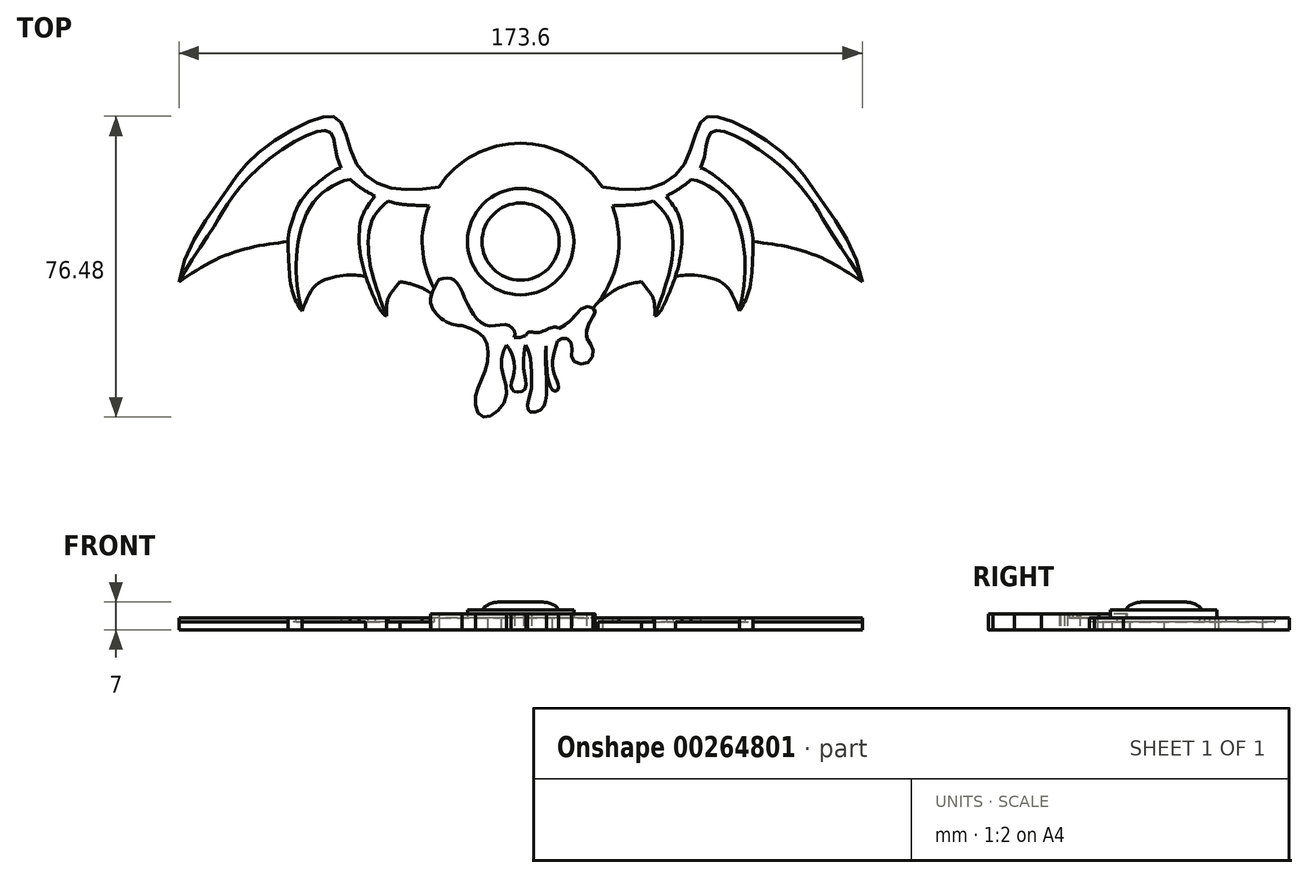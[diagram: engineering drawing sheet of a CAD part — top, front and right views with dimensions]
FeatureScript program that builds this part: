
annotation { "Feature Type Name" : "Feature", "Feature Type Description" : "" }
export const myFeature = defineFeature(function(context is Context, id is Id, definition is map)
    precondition{}
    {
        {
            var Q0;
            Q0=qCreatedBy(makeId("Top.planeOp"),FACE);
            var sketch = newSketch(context, id + "F0", { "sketchPlane" : qUnion([Q0])});
            skCircle(sketch, "E0", {"center": v(0, 0) * mm, "radius": 25 * mm});
            skLineSegment(sketch, "E1", {"start": v(0, 25) * mm, "end": v(0, -25) * mm, "construction": true});
            skFitSpline(sketch, "E2", {"points": [v(20.76, 13.92) * mm, v(34.08, 13.92) * mm, v(42, 20.48) * mm, v(46, 30.69) * mm, v(50.93, 31.48) * mm, v(67.03, 22.24) * mm, v(75.74, 11.46) * mm, v(86.8, -10.28) * mm], "startDerivative": vector(95.75, -17.53) * mm, "endDerivative": vector(18.54, -135.11) * mm});
            skFitSpline(sketch, "E3", {"points": [v(20.7, -14) * mm, v(37, -10.54) * mm, v(45, -8.07) * mm, v(66.66, 1.74) * mm, v(75.74, 11.46) * mm], "startDerivative": vector(59.46, -0.59) * mm, "endDerivative": vector(18.77, 28.66) * mm, "construction": true});
            skFitSpline(sketch, "E4", {"points": [v(23.3, 9.08) * mm, v(33.72, 10.28) * mm, v(45.64, 18.76) * mm, v(47.9, 27.18) * mm, v(51.1, 28.14) * mm, v(65.44, 19.69) * mm, v(74.45, 9.58) * mm, v(78.2, 3.43) * mm, v(86.8, -10.28) * mm], "startDerivative": vector(110.38, 5.87) * mm, "endDerivative": vector(40.39, -81.17) * mm});
            skFitSpline(sketch, "E5", {"points": [v(33.72, 10.28) * mm, v(37.86, 5.02) * mm, v(38.5, -3.9) * mm, v(37, -10.54) * mm, v(34.08, -18.9) * mm], "startDerivative": vector(21.3, -19.5) * mm, "endDerivative": vector(-13.55, -34.2) * mm});
            skFitSpline(sketch, "E6", {"points": [v(37, 11.6) * mm, v(40.25, 6.46) * mm, v(40.52, -4.24) * mm, v(37.2, -14.33) * mm, v(34.08, -18.9) * mm], "startDerivative": vector(14.85, -22) * mm, "endDerivative": vector(-16.96, -5.17) * mm});
            skFitSpline(sketch, "E7", {"points": [v(32.11, -12.01) * mm, v(33.72, -14.49) * mm, v(34.08, -18.9) * mm], "startDerivative": vector(4.43, -5.79) * mm, "endDerivative": vector(-0.15, -8.8) * mm});
            skFitSpline(sketch, "E8", {"points": [v(45.64, 18.76) * mm, v(50.26, 15.97) * mm, v(55.72, 10.44) * mm, v(58.9, 2) * mm, v(59.02, -2.64) * mm, v(58.1, -12.2) * mm, v(55.56, -17.62) * mm], "startDerivative": vector(28.21, -5.42) * mm, "endDerivative": vector(-19.1, -30.2) * mm});
            skFitSpline(sketch, "E9", {"points": [v(43.34, 15.84) * mm, v(49.55, 13.02) * mm, v(53.96, 7.9) * mm, v(56.67, -1.36) * mm, v(56.83, -10.28) * mm, v(55.56, -17.62) * mm], "startDerivative": vector(32.47, -4.35) * mm, "endDerivative": vector(-7.91, -36.84) * mm});
            skFitSpline(sketch, "E10", {"points": [v(38.97, -9.94) * mm, v(46.63, -10.28) * mm, v(52.84, -13.22) * mm, v(55.56, -17.62) * mm], "startDerivative": vector(21.38, 0.7) * mm, "endDerivative": vector(7.12, -15.9) * mm, "construction": true});
            skFitSpline(sketch, "E11", {"points": [v(59.1, 0) * mm, v(68, -1.36) * mm, v(77.72, -4.7) * mm, v(86.8, -10.28) * mm], "startDerivative": vector(27.78, -3.23) * mm, "endDerivative": vector(25.67, -17.5) * mm});
            skFitSpline(sketch, "E12", {"points": [v(19.62, -15.5) * mm, v(25.1, -11.72) * mm, v(30.69, -10.12) * mm], "startDerivative": vector(10.4, 8.3) * mm, "endDerivative": vector(11.78, 2.35) * mm});
            skFitSpline(sketch, "E13", {"points": [v(32.11, -12.01) * mm, v(30.69, -10.12) * mm], "startDerivative": vector(-1.42, 1.9) * mm, "endDerivative": vector(-1.42, 1.9) * mm});
            skFitSpline(sketch, "E14", {"points": [v(55.56, -17.62) * mm, v(52.05, -11.08) * mm, v(46.6, -8.83) * mm, v(42.13, -8.5) * mm, v(39.36, -8.79) * mm], "startDerivative": vector(-10.96, 25.87) * mm, "endDerivative": vector(-14.04, -2.02) * mm});
            skFitSpline(sketch, "E15", {"points": [v(20.76, 13.92) * mm, v(16.18, 9.49) * mm, v(19.62, -15.5) * mm], "startDerivative": vector(-16.85, -9.2) * mm, "endDerivative": vector(11.44, -45.62) * mm});
            skFitSpline(sketch, "E16.MirrorCS", {"points": [v(-20.76, 13.92) * mm, v(-16.18, 9.49) * mm, v(-19.62, -15.5) * mm], "startDerivative": vector(16.85, -9.2) * mm, "endDerivative": vector(-11.44, -45.62) * mm});
            skFitSpline(sketch, "E17.MirrorCS", {"points": [v(-23.3, 9.08) * mm, v(-33.72, 10.28) * mm, v(-45.64, 18.76) * mm, v(-47.9, 27.18) * mm, v(-51.1, 28.14) * mm, v(-65.44, 19.69) * mm, v(-74.45, 9.58) * mm, v(-78.2, 3.43) * mm, v(-86.8, -10.28) * mm], "startDerivative": vector(-110.38, 5.87) * mm, "endDerivative": vector(-40.39, -81.17) * mm});
            skFitSpline(sketch, "E18.MirrorCS", {"points": [v(-20.76, 13.92) * mm, v(-34.08, 13.92) * mm, v(-42, 20.48) * mm, v(-46, 30.69) * mm, v(-50.93, 31.48) * mm, v(-67.03, 22.24) * mm, v(-75.74, 11.46) * mm, v(-86.8, -10.28) * mm], "startDerivative": vector(-95.75, -17.53) * mm, "endDerivative": vector(-18.54, -135.11) * mm});
            skFitSpline(sketch, "E19.MirrorCS", {"points": [v(-33.72, 10.28) * mm, v(-37.86, 5.02) * mm, v(-38.5, -3.9) * mm, v(-37, -10.54) * mm, v(-34.08, -18.9) * mm], "startDerivative": vector(-21.3, -19.5) * mm, "endDerivative": vector(13.55, -34.2) * mm});
            skFitSpline(sketch, "E20.MirrorCS", {"points": [v(-37, 11.6) * mm, v(-40.25, 6.46) * mm, v(-40.52, -4.24) * mm, v(-37.2, -14.33) * mm, v(-34.08, -18.9) * mm], "startDerivative": vector(-14.85, -22) * mm, "endDerivative": vector(16.96, -5.17) * mm});
            skFitSpline(sketch, "E21.MirrorCS", {"points": [v(-43.34, 15.84) * mm, v(-49.55, 13.02) * mm, v(-53.96, 7.9) * mm, v(-56.67, -1.36) * mm, v(-56.83, -10.28) * mm, v(-55.56, -17.62) * mm], "startDerivative": vector(-32.47, -4.35) * mm, "endDerivative": vector(7.91, -36.84) * mm});
            skFitSpline(sketch, "E22.MirrorCS", {"points": [v(-45.64, 18.76) * mm, v(-50.26, 15.97) * mm, v(-55.72, 10.44) * mm, v(-58.9, 2) * mm, v(-59.02, -2.64) * mm, v(-58.1, -12.2) * mm, v(-55.56, -17.62) * mm], "startDerivative": vector(-28.21, -5.42) * mm, "endDerivative": vector(19.1, -30.2) * mm});
            skFitSpline(sketch, "E23.MirrorCS", {"points": [v(-19.62, -15.5) * mm, v(-25.1, -11.72) * mm, v(-30.69, -10.12) * mm], "startDerivative": vector(-10.4, 8.3) * mm, "endDerivative": vector(-11.78, 2.35) * mm});
            skFitSpline(sketch, "E24.MirrorCS", {"points": [v(-32.11, -12.01) * mm, v(-30.69, -10.12) * mm], "startDerivative": vector(1.42, 1.9) * mm, "endDerivative": vector(1.42, 1.9) * mm});
            skFitSpline(sketch, "E25.MirrorCS", {"points": [v(-32.11, -12.01) * mm, v(-33.72, -14.49) * mm, v(-34.08, -18.9) * mm], "startDerivative": vector(-4.43, -5.79) * mm, "endDerivative": vector(0.15, -8.8) * mm});
            skFitSpline(sketch, "E26.MirrorCS", {"points": [v(-59.1, 0) * mm, v(-68, -1.36) * mm, v(-77.72, -4.7) * mm, v(-86.8, -10.28) * mm], "startDerivative": vector(-27.78, -3.23) * mm, "endDerivative": vector(-25.67, -17.5) * mm});
            skFitSpline(sketch, "E27.MirrorCS", {"points": [v(-55.56, -17.62) * mm, v(-52.05, -11.08) * mm, v(-46.6, -8.83) * mm, v(-42.13, -8.5) * mm, v(-39.36, -8.79) * mm], "startDerivative": vector(10.96, 25.87) * mm, "endDerivative": vector(14.04, -2.02) * mm});
            skSolve(sketch);
        }
        {
            var Q0;
            {var subQ0=sQuery(id+"F0.wireOp",EDGE,"E15");Q0=makeQuery(id+"F0.imprint","IMPRINT",FACE,{"disambiguationData":[TD([[makeQuery(id+"F0.imprint","IMPRINT",EDGE,{"derivedFrom":subQ0}),-1.0]])]});}
            var Q1;
            {var subQ0=sQuery(id+"F0.wireOp",EDGE,"E15");Q1=makeQuery(id+"F0.imprint","IMPRINT",FACE,{"disambiguationData":[TD([[makeQuery(id+"F0.imprint","IMPRINT",EDGE,{"derivedFrom":subQ0}),1.0]])]});}
            var Q2;
            {var subQ0=sQuery(id+"F0.wireOp",EDGE,"E16.MirrorCS");Q2=makeQuery(id+"F0.imprint","IMPRINT",FACE,{"disambiguationData":[TD([[makeQuery(id+"F0.imprint","IMPRINT",EDGE,{"derivedFrom":subQ0}),-1.0]])]});}
            extrude(context, id + "F1", {"entities" : qUnion([Q0, Q1, Q2]), "depth" : 3 * mm, "offsetDistance" : 25 * mm});
        }
        {
            var Q0;
            Q0=qCreatedBy(makeId("Top.planeOp"),FACE);
            var sketch = newSketch(context, id + "F2", { "sketchPlane" : qUnion([Q0])});
            skCircle(sketch, "E28", {"center": v(0, 0) * mm, "radius": 13.5 * mm});
            skSolve(sketch);
        }
        {
            var Q0;
            Q0=qSketchRegion(id+"F2",true);
            extrude(context, id + "F3", {"entities" : qUnion([Q0]), "operationType" : NewBodyOperationType.ADD, "depth" : 5 * mm, "offsetDistance" : 25 * mm});
        }
        {
            var Q0;
            Q0=qCreatedBy(makeId("Top.planeOp"),FACE);
            var sketch = newSketch(context, id + "F4", { "sketchPlane" : qUnion([Q0])});
            skCircle(sketch, "E29", {"center": v(0, 0) * mm, "radius": 9.8 * mm});
            skSolve(sketch);
        }
        {
            var Q0;
            Q0=qSketchRegion(id+"F4",true);
            var Q1;
            Q1=qConstructionFilter(qBodyType(qCreatedBy(id+"F4",EDGE),BodyType.WIRE),ConstructionObject.NO);
            extrude(context, id + "F5", {"entities" : qUnion([Q0]), "operationType" : NewBodyOperationType.ADD, "surfaceEntities" : qUnion([Q1]), "depth" : 7 * mm, "offsetDistance" : 25 * mm});
        }
        {
            var Q0;
            Q0=makeQuery(id+"F5.opExtrude","CAP_FACE",FACE,{"disambiguationData":[OSD([sQuery(id+"F4.wireOp",EDGE,"E29")])],"isStart":false});
            fillet(context, id + "F6", {"entities" : qUnion([Q0]), "radius" : 5 * mm, "tangentPropagation" : true, "allowEdgeOverflow" : false});
        }
        {
            var Q0;
            {var subQ4=sQuery(id+"F0.wireOp",EDGE,"E2");Q0=makeQuery(id+"F0.imprint","IMPRINT",FACE,{"disambiguationData":[TD([[makeQuery(id+"F0.imprint","IMPRINT",EDGE,{"derivedFrom":subQ4}),-1.0]])]});}
            var Q1;
            {var subQ0=sQuery(id+"F0.wireOp",EDGE,"E15");Q1=makeQuery(id+"F0.imprint","IMPRINT",FACE,{"disambiguationData":[TD([[makeQuery(id+"F0.imprint","IMPRINT",EDGE,{"derivedFrom":subQ0}),1.0]])]});}
            var Q2;
            {var subQ0=sQuery(id+"F0.wireOp",EDGE,"E5");Q2=makeQuery(id+"F0.imprint","IMPRINT",FACE,{"disambiguationData":[TD([[makeQuery(id+"F0.imprint","IMPRINT",EDGE,{"derivedFrom":subQ0}),-1.0]])]});}
            var Q3;
            {var subQ0=sQuery(id+"F0.wireOp",EDGE,"E5");Q3=makeQuery(id+"F0.imprint","IMPRINT",FACE,{"disambiguationData":[TD([[makeQuery(id+"F0.imprint","IMPRINT",EDGE,{"derivedFrom":subQ0}),1.0]])]});}
            var Q4;
            {var subQ3=sQuery(id+"F0.wireOp",EDGE,"E9");Q4=makeQuery(id+"F0.imprint","IMPRINT",FACE,{"disambiguationData":[TD([[makeQuery(id+"F0.imprint","IMPRINT",EDGE,{"derivedFrom":subQ3}),-1.0]])]});}
            var Q5;
            {var subQ3=sQuery(id+"F0.wireOp",EDGE,"E9");Q5=makeQuery(id+"F0.imprint","IMPRINT",FACE,{"disambiguationData":[TD([[makeQuery(id+"F0.imprint","IMPRINT",EDGE,{"derivedFrom":subQ3}),1.0]])]});}
            var Q6;
            {var subQ0=sQuery(id+"F0.wireOp",EDGE,"E11");Q6=makeQuery(id+"F0.imprint","IMPRINT",FACE,{"disambiguationData":[TD([[makeQuery(id+"F0.imprint","IMPRINT",EDGE,{"derivedFrom":subQ0}),1.0]])]});}
            var Q7;
            {var subQ1=sQuery(id+"F0.wireOp",EDGE,"E19.MirrorCS");Q7=makeQuery(id+"F0.imprint","IMPRINT",FACE,{"disambiguationData":[TD([[makeQuery(id+"F0.imprint","IMPRINT",EDGE,{"derivedFrom":subQ1}),1.0]])]});}
            var Q8;
            {var subQ3=sQuery(id+"F0.wireOp",EDGE,"E21.MirrorCS");Q8=makeQuery(id+"F0.imprint","IMPRINT",FACE,{"disambiguationData":[TD([[makeQuery(id+"F0.imprint","IMPRINT",EDGE,{"derivedFrom":subQ3}),1.0]])]});}
            var Q9;
            {var subQ0=sQuery(id+"F0.wireOp",EDGE,"E19.MirrorCS");Q9=makeQuery(id+"F0.imprint","IMPRINT",FACE,{"disambiguationData":[TD([[makeQuery(id+"F0.imprint","IMPRINT",EDGE,{"derivedFrom":subQ0}),-1.0]])]});}
            var Q10;
            {var subQ6=sQuery(id+"F0.wireOp",EDGE,"E18.MirrorCS");Q10=makeQuery(id+"F0.imprint","IMPRINT",FACE,{"disambiguationData":[TD([[makeQuery(id+"F0.imprint","IMPRINT",EDGE,{"derivedFrom":subQ6}),1.0]])]});}
            var Q11;
            {var subQ0=sQuery(id+"F0.wireOp",EDGE,"E26.MirrorCS");Q11=makeQuery(id+"F0.imprint","IMPRINT",FACE,{"disambiguationData":[TD([[makeQuery(id+"F0.imprint","IMPRINT",EDGE,{"derivedFrom":subQ0}),-1.0]])]});}
            var Q12;
            {var subQ0=sQuery(id+"F0.wireOp",EDGE,"E21.MirrorCS");Q12=makeQuery(id+"F0.imprint","IMPRINT",FACE,{"disambiguationData":[TD([[makeQuery(id+"F0.imprint","IMPRINT",EDGE,{"derivedFrom":subQ0}),-1.0]])]});}
            var Q13;
            {var subQ0=sQuery(id+"F0.wireOp",EDGE,"E16.MirrorCS");Q13=makeQuery(id+"F0.imprint","IMPRINT",FACE,{"disambiguationData":[TD([[makeQuery(id+"F0.imprint","IMPRINT",EDGE,{"derivedFrom":subQ0}),-1.0]])]});}
            extrude(context, id + "F7", {"entities" : qUnion([Q0, Q1, Q2, Q3, Q4, Q5, Q6, Q7, Q8, Q9, Q10, Q11, Q12, Q13]), "operationType" : NewBodyOperationType.ADD, "depth" : 2 * mm, "offsetDistance" : 25 * mm});
        }
        {
            var Q0;
            {var subQ4=sQuery(id+"F0.wireOp",EDGE,"E2");Q0=makeQuery(id+"F0.imprint","IMPRINT",FACE,{"disambiguationData":[TD([[makeQuery(id+"F0.imprint","IMPRINT",EDGE,{"derivedFrom":subQ4}),-1.0]])]});}
            var Q1;
            {var subQ0=sQuery(id+"F0.wireOp",EDGE,"E5");Q1=makeQuery(id+"F0.imprint","IMPRINT",FACE,{"disambiguationData":[TD([[makeQuery(id+"F0.imprint","IMPRINT",EDGE,{"derivedFrom":subQ0}),1.0]])]});}
            var Q2;
            {var subQ3=sQuery(id+"F0.wireOp",EDGE,"E9");Q2=makeQuery(id+"F0.imprint","IMPRINT",FACE,{"disambiguationData":[TD([[makeQuery(id+"F0.imprint","IMPRINT",EDGE,{"derivedFrom":subQ3}),1.0]])]});}
            var Q3;
            {var subQ6=sQuery(id+"F0.wireOp",EDGE,"E18.MirrorCS");Q3=makeQuery(id+"F0.imprint","IMPRINT",FACE,{"disambiguationData":[TD([[makeQuery(id+"F0.imprint","IMPRINT",EDGE,{"derivedFrom":subQ6}),1.0]])]});}
            var Q4;
            {var subQ0=sQuery(id+"F0.wireOp",EDGE,"E19.MirrorCS");Q4=makeQuery(id+"F0.imprint","IMPRINT",FACE,{"disambiguationData":[TD([[makeQuery(id+"F0.imprint","IMPRINT",EDGE,{"derivedFrom":subQ0}),-1.0]])]});}
            var Q5;
            {var subQ0=sQuery(id+"F0.wireOp",EDGE,"E21.MirrorCS");Q5=makeQuery(id+"F0.imprint","IMPRINT",FACE,{"disambiguationData":[TD([[makeQuery(id+"F0.imprint","IMPRINT",EDGE,{"derivedFrom":subQ0}),-1.0]])]});}
            extrude(context, id + "F8", {"entities" : qUnion([Q0, Q1, Q2, Q3, Q4, Q5]), "operationType" : NewBodyOperationType.ADD, "depth" : 3 * mm, "offsetDistance" : 25 * mm});
        }
        {
            var Q0;
            Q0=qCreatedBy(makeId("Top.planeOp"),FACE);
            var sketch = newSketch(context, id + "F9", { "sketchPlane" : qUnion([Q0])});
            skFitSpline(sketch, "E30", {"points": [v(-20.72, -9.64) * mm, v(-22.8, -15.86) * mm, v(-18.33, -20.64) * mm, v(-14.83, -21.28) * mm], "startDerivative": vector(-10.43, -17.24) * mm, "endDerivative": vector(12.17, -0.13) * mm});
            skFitSpline(sketch, "E31", {"points": [v(-20.72, -9.64) * mm, v(-17.06, -9.64) * mm, v(-13.55, -15.7) * mm, v(-8.6, -21.28) * mm, v(-3.03, -21.28) * mm, v(-1.44, -23.83) * mm, v(-3.5, -26.22) * mm, v(-4.78, -32.28) * mm, v(-3.83, -40.1) * mm, v(-9.4, -44.56) * mm, v(-11.48, -39.61) * mm, v(-8.77, -31.96) * mm, v(-9.25, -24.47) * mm, v(-14.83, -21.28) * mm], "startDerivative": vector(65.16, 15.52) * mm, "endDerivative": vector(-82.7, 27.37) * mm});
            skFitSpline(sketch, "E32", {"points": [v(-3.5, -26.22) * mm, v(-1.91, -29.41) * mm, v(-1.75, -33.72) * mm, v(-2.4, -36.9) * mm, v(-1.4, -38.14) * mm, v(1.08, -37.54) * mm, v(0.92, -33.52) * mm, v(0.76, -29.33) * mm, v(1.27, -25.74) * mm, v(1.2, -23.95) * mm, v(0, -24.31) * mm, v(-1.64, -24.31) * mm], "startDerivative": vector(18.13, -28.93) * mm, "endDerivative": vector(-23.4, 3.66) * mm});
            skFitSpline(sketch, "E33", {"points": [v(1.2, -23.95) * mm, v(2.14, -22.96) * mm, v(4.4, -23.08) * mm, v(7.95, -21.84) * mm, v(9.81, -22.12) * mm, v(8.9, -26.63) * mm, v(8.29, -32.94) * mm, v(9.64, -36.71) * mm, v(8.96, -37.95) * mm, v(7.5, -36.77) * mm, v(6.41, -26.5) * mm], "startDerivative": vector(11.67, 19.38) * mm, "endDerivative": vector(-1.14, 43.55) * mm});
            skFitSpline(sketch, "E34", {"points": [v(1.2, -26.22) * mm, v(2.1, -28.1) * mm, v(2.77, -32.66) * mm, v(2.49, -38.68) * mm, v(1.73, -41.67) * mm, v(2.36, -43.24) * mm, v(5.02, -42.75) * mm, v(6.41, -40.17) * mm, v(6.5, -34.48) * mm, v(6.41, -26.5) * mm], "startDerivative": vector(11, -19.03) * mm, "endDerivative": vector(3.74, 33.89) * mm});
            skFitSpline(sketch, "E35", {"points": [v(9.81, -22.12) * mm, v(13.2, -19.51) * mm, v(16.5, -16.57) * mm, v(18.88, -17.43) * mm, v(17.55, -20.46) * mm, v(16.89, -24.53) * mm, v(18.4, -27.47) * mm, v(16.89, -30.8) * mm, v(13.2, -29.94) * mm, v(13.1, -26.43) * mm, v(11.39, -24.53) * mm, v(9.34, -25.28) * mm], "startDerivative": vector(34.2, 22.05) * mm, "endDerivative": vector(-27.8, -17.8) * mm});
            skSolve(sketch);
        }
        {
            var Q0;
            {var subQ0=sQuery(id+"F9.wireOp",EDGE,"E30");Q0=makeQuery(id+"F9.imprint","IMPRINT",FACE,{"disambiguationData":[TD([[makeQuery(id+"F9.imprint","IMPRINT",EDGE,{"derivedFrom":subQ0}),1.0]])]});}
            var Q1;
            {var subQ0=sQuery(id+"F9.wireOp",EDGE,"E32");var subQ1=sQuery(id+"F9.wireOp",EDGE,"E31");var subQ2=makeQuery(id+"F9.imprint","INTERSECT",VERTEX,{"disambiguationData":[OD(0.0)],"derivedFrom":[subQ1,subQ0]});Q1=makeQuery(id+"F9.imprint","IMPRINT",FACE,{"disambiguationData":[TD([[makeQuery(id+"F9.imprint","IMPRINT",EDGE,{"disambiguationData":[TD([[subQ2,1.0]])],"derivedFrom":subQ1}),1.0]])]});}
            var Q2;
            {var subQ0=sQuery(id+"F9.wireOp",EDGE,"E34");Q2=makeQuery(id+"F9.imprint","IMPRINT",FACE,{"disambiguationData":[TD([[makeQuery(id+"F9.imprint","IMPRINT",EDGE,{"derivedFrom":subQ0}),1.0]])]});}
            var Q3;
            {var subQ0=sQuery(id+"F9.wireOp",EDGE,"E35");Q3=makeQuery(id+"F9.imprint","IMPRINT",FACE,{"disambiguationData":[TD([[makeQuery(id+"F9.imprint","IMPRINT",EDGE,{"derivedFrom":subQ0}),-1.0]])]});}
            extrude(context, id + "F10", {"entities" : qUnion([Q0, Q1, Q2, Q3]), "operationType" : NewBodyOperationType.ADD, "depth" : 4 * mm, "offsetDistance" : 25 * mm});
        }
    });
